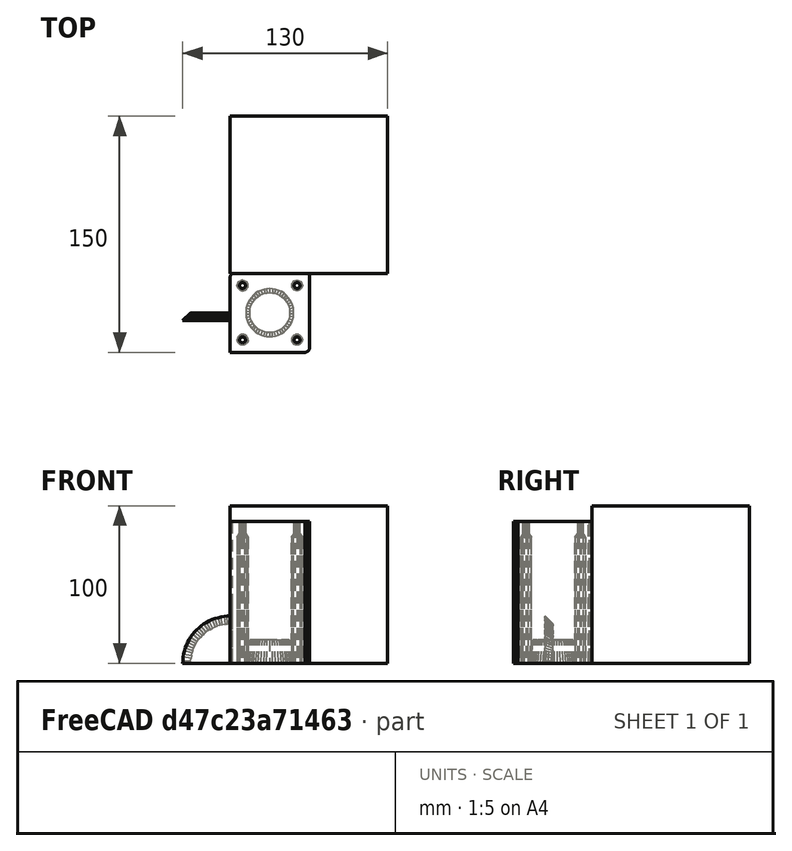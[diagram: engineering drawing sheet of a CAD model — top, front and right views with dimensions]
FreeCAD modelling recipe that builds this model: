
FCSTD DOCUMENT  (FreeCAD 0.17R13541 (Git))
Label: front right
License: All rights reserved
LicenseURL: http://en.wikipedia.org/wiki/All_rights_reserved
objects: App::MeasureDistance×2, Part::Feature×1, Part::Box×1, Part::FeaturePython×1
note: 3 computed .brp shape members not serialized (recipe doc carries the construction recipe); baked Part::Feature solids carry a one-line shape summary decoded from their .brp

FEATURE [App::MeasureDistance] Distance  label="Distance: 20,10 mm"
  Distance = 20.1
  P1 = (50.5,50.5,90)
  P2 = (30.4,50.5,90)
FEATURE [App::MeasureDistance] Distance001  label="Distance: 22,40 mm"
  Distance = 22.4
  P1 = (25.4,50.5,90)
  P2 = (3,50.5,90)
FEATURE [Part::Feature] Leg_extension_front_right001_solid  label="Leg_extension_front_right001 (Solid)"
  shape: bbox 80.5 x 80.5 x 90 mm, 1300 faces (baked)
FEATURE [Part::Box] Box  label="Cube"
  AttacherType = Attacher::AttachEngine3D
  Height = 100
  Length = 100
  Placement = pos=(0,50,0) rot=(0,0,1;0rad)
  Width = 100
FEATURE [Part::FeaturePython] Slice  # WARN: FeaturePython — macro-defined, semantics opaque (R4)
  Base = -> Leg_extension_front_right001_solid
  Mode = 1
  Tolerance = 0
  Tools = -> [Box]
